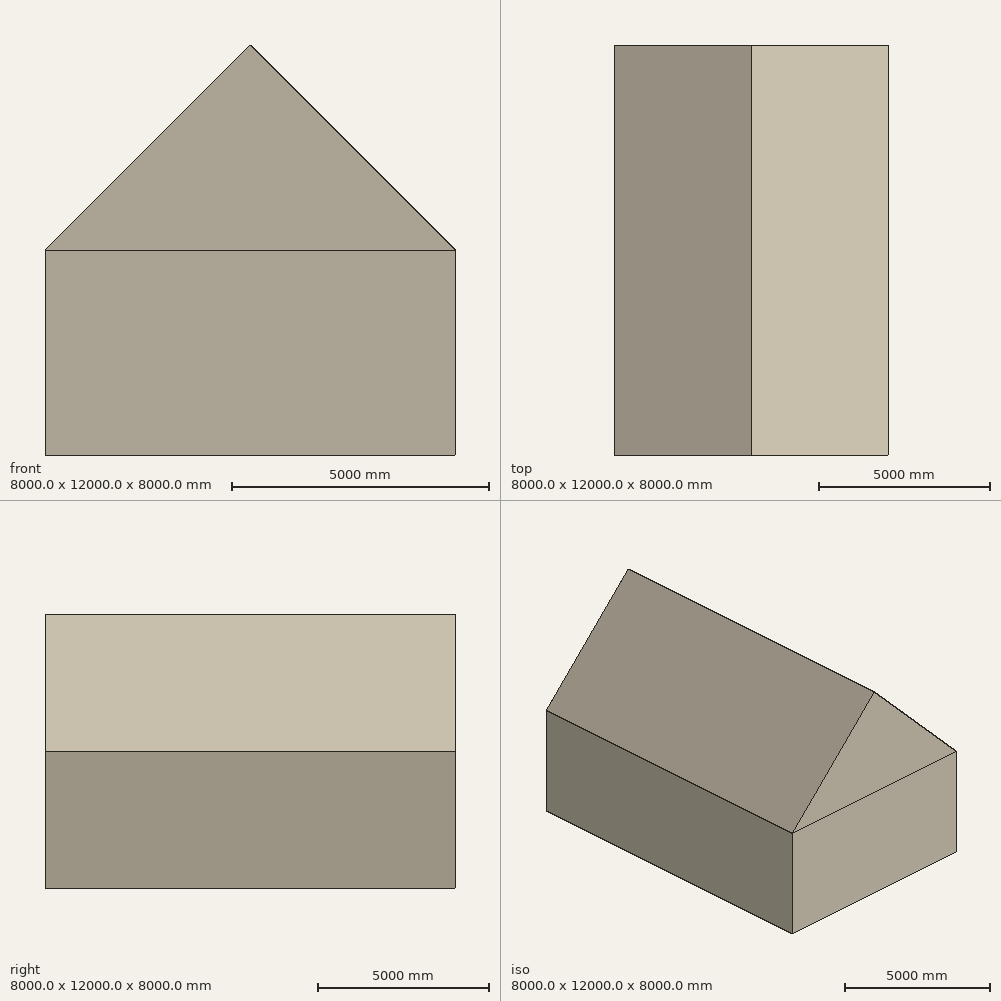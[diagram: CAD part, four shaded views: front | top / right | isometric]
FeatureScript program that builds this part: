
annotation { "Feature Type Name" : "Feature", "Feature Type Description" : "" }
export const myFeature = defineFeature(function(context is Context, id is Id, definition is map)
    precondition{}
    {
        {
            var Q0;
            Q0=qCreatedBy(makeId("Front.planeOp"),FACE);
            var sketch = newSketch(context, id + "F0", { "sketchPlane" : qUnion([Q0])});
            skLineSegment(sketch, "E0", {"start": v(0, 0) * mm, "end": v(8000, 0) * mm});
            skLineSegment(sketch, "E1", {"start": v(8000, 0) * mm, "end": v(8000, 4000) * mm});
            skLineSegment(sketch, "E2", {"start": v(0, 4000) * mm, "end": v(0, 0) * mm});
            skLineSegment(sketch, "E3", {"start": v(0, 4000) * mm, "end": v(4265.68, 4000) * mm});
            skLineSegment(sketch, "E4", {"start": v(4265.68, 4000) * mm, "end": v(8000, 4000) * mm});
            skLineSegment(sketch, "E5", {"start": v(0, 4000) * mm, "end": v(4000, 4000) * mm});
            skLineSegment(sketch, "E6", {"start": v(4000, 4000) * mm, "end": v(8000, 4000) * mm});
            skSolve(sketch);
        }
        {
            var Q0;
            Q0=makeQuery(id+"F0.imprint","IMPRINT",FACE,{"disambiguationData":[TD([[makeQuery(id+"F0.imprint","IMPRINT",EDGE,{"derivedFrom":sQuery(id+"F0.wireOp",EDGE,"E0")}),1.0]])]});
            var Q1;
            Q1=makeQuery(id+"F0.imprint","IMPRINT",FACE,{"disambiguationData":[TD([[makeQuery(id+"F0.imprint","IMPRINT",EDGE,{"derivedFrom":sQuery(id+"F0.wireOp",EDGE,"E3")}),1.0]])]});
            extrude(context, id + "F1", {"entities" : qUnion([Q0, Q1]), "depth" : 12000 * mm});
        }
        {
            var Q0;
            Q0=makeQuery(id+"F1.opExtrude","CAP_FACE",FACE,{"disambiguationData":[OSD([sQuery(id+"F0.wireOp",EDGE,"E0"),sQuery(id+"F0.wireOp",EDGE,"E1"),sQuery(id+"F0.wireOp",EDGE,"E2"),sQuery(id+"F0.wireOp",EDGE,"E5"),sQuery(id+"F0.wireOp",EDGE,"E6")])],"isStart":false});
            var sketch = newSketch(context, id + "F2", { "sketchPlane" : qUnion([Q0])});
            skLineSegment(sketch, "E7", {"start": v(4000, 4000) * mm, "end": v(4000, 8000) * mm});
            skLineSegment(sketch, "E8", {"start": v(4000, 8000) * mm, "end": v(8000, 4000) * mm});
            skLineSegment(sketch, "E9", {"start": v(4000, 8000) * mm, "end": v(0, 4000) * mm});
            skSolve(sketch);
        }
        {
            var Q0;
            {var subQ0=sQuery(id+"F2.wireOp",EDGE,"E7");Q0=makeQuery(id+"F2.imprint","IMPRINT",FACE,{"disambiguationData":[TD([[makeQuery(id+"F2.imprint","IMPRINT",EDGE,{"derivedFrom":subQ0}),-1.0]])]});}
            var Q1;
            {var subQ0=sQuery(id+"F2.wireOp",EDGE,"E7");Q1=makeQuery(id+"F2.imprint","IMPRINT",FACE,{"disambiguationData":[TD([[makeQuery(id+"F2.imprint","IMPRINT",EDGE,{"derivedFrom":subQ0}),1.0]])]});}
            extrude(context, id + "F3", {"entities" : qUnion([Q0, Q1]), "oppositeDirection" : true, "depth" : 12000 * mm});
        }
    });
